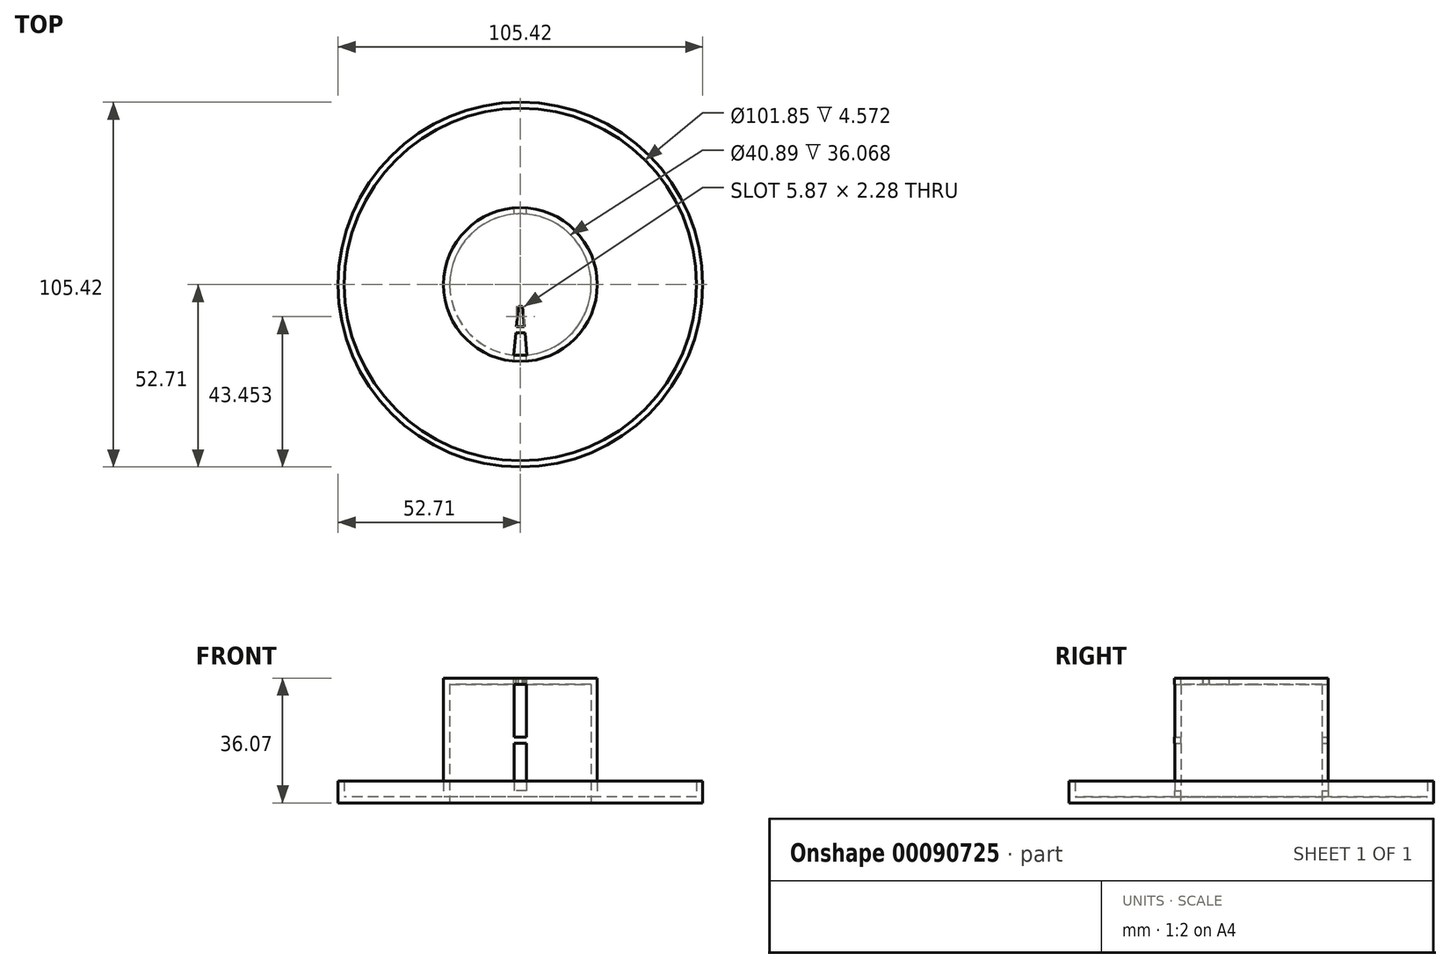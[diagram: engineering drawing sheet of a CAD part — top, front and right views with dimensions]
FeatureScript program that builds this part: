
annotation { "Feature Type Name" : "Feature", "Feature Type Description" : "" }
export const myFeature = defineFeature(function(context is Context, id is Id, definition is map)
    precondition{}
    {
        {
            var Q0;
            Q0=qCreatedBy(makeId("Top.planeOp"),FACE);
            var sketch = newSketch(context, id + "F0", { "sketchPlane" : qUnion([Q0])});
            skCircle(sketch, "E0", {"center": v(0, 0) * mm, "radius": 52.7 * mm});
            skSolve(sketch);
        }
        {
            var Q0;
            Q0 = qSketchRegion(id + "F0", true);
            extrude(context, id + "F1", {"entities" : qUnion([Q0]), "depth" : 6.35 * mm});
        }
        {
            var Q0;
            Q0=makeQuery(id+"F1.opExtrude","CAP_FACE",FACE,{"disambiguationData":[OSD([sQuery(id+"F0.wireOp",EDGE,"E0")])],"isStart":false});
            shell(context, id + "F2", {"entities" : qUnion([Q0]), "thickness" : 1.78 * mm});
        }
        {
            var Q0;
            {var subQ0=sQuery(id+"F0.wireOp",EDGE,"E0");Q0=makeQuery(id+"F2.opShell","OFFSET_FACE",FACE,{"disambiguationData":[OSD([subQ0]),TDD([makeQuery(id+"F1.opExtrude","CAP_FACE",FACE,{"disambiguationData":[OSD([subQ0])],"isStart":true})])]});}
            var sketch = newSketch(context, id + "F3", { "sketchPlane" : qUnion([Q0])});
            skCircle(sketch, "E1", {"center": v(0, 0) * mm, "radius": 22.23 * mm});
            skSolve(sketch);
        }
        {
            var Q0;
            Q0 = qSketchRegion(id + "F3", true);
            extrude(context, id + "F4", {"entities" : qUnion([Q0]), "operationType" : NewBodyOperationType.ADD, "depth" : 34.3 * mm});
        }
        {
            var Q0;
            Q0=qCreatedBy(makeId("Front.planeOp"),FACE);
            var sketch = newSketch(context, id + "F5", { "sketchPlane" : qUnion([Q0])});
            skLineSegment(sketch, "E2.bottom", {"start": v(-1.78, 34.3) * mm, "end": v(1.78, 34.3) * mm});
            skLineSegment(sketch, "E2.top", {"start": v(-1.78, 19.05) * mm, "end": v(1.78, 19.05) * mm});
            skLineSegment(sketch, "E2.left", {"start": v(-1.78, 34.3) * mm, "end": v(-1.78, 19.05) * mm});
            skLineSegment(sketch, "E2.right", {"start": v(1.78, 34.3) * mm, "end": v(1.78, 19.05) * mm});
            skLineSegment(sketch, "E3.bottom", {"start": v(-1.78, 17.27) * mm, "end": v(1.78, 17.27) * mm});
            skLineSegment(sketch, "E3.top", {"start": v(-1.78, 3.56) * mm, "end": v(1.78, 3.56) * mm});
            skLineSegment(sketch, "E3.left", {"start": v(-1.78, 17.27) * mm, "end": v(-1.78, 3.56) * mm});
            skLineSegment(sketch, "E3.right", {"start": v(1.78, 17.27) * mm, "end": v(1.78, 3.56) * mm});
            skSolve(sketch);
        }
        {
            var Q0;
            Q0 = qSketchRegion(id + "F5", true);
            var Q1;
            Q1=makeQuery(id+"F4.opExtrude","SWEPT_FACE",FACE,{"disambiguationData":[OSD([sQuery(id+"F3.wireOp",EDGE,"E1")])]});
            extrude(context, id + "F6", {"entities" : qUnion([Q0]), "operationType" : NewBodyOperationType.REMOVE, "endBoundEntityFace" : qUnion([Q1]), "depth" : 50.8 * mm, "symmetric" : true});
        }
        {
            var Q0;
            Q0=makeQuery(id+"F1.opExtrude","CAP_FACE",FACE,{"disambiguationData":[OSD([sQuery(id+"F0.wireOp",EDGE,"E0")])],"isStart":true});
            var sketch = newSketch(context, id + "F7", { "sketchPlane" : qUnion([Q0])});
            skCircle(sketch, "E4.0", {"center": v(0, 0) * mm, "radius": 22.23 * mm, "construction": true});
            skCircle(sketch, "E5.0", {"center": v(0, 0) * mm, "radius": 20.45 * mm});
            skSolve(sketch);
        }
        {
            var Q0;
            Q0 = qSketchRegion(id + "F7", true);
            extrude(context, id + "F8", {"entities" : qUnion([Q0]), "operationType" : NewBodyOperationType.REMOVE, "oppositeDirection" : true, "depth" : 34.3 * mm});
        }
        {
            var Q0;
            Q0=makeQuery(id+"F4.opExtrude","CAP_FACE",FACE,{"disambiguationData":[OSD([sQuery(id+"F3.wireOp",EDGE,"E1")])],"isStart":false});
            var sketch = newSketch(context, id + "F9", { "sketchPlane" : qUnion([Q0])});
            skArc(sketch, "E6.0", {"start": v(-1.78, -22.15) * mm, "mid": v(0, -22.23) * mm, "end": v(1.78, -22.15) * mm, "construction": true});
            skArc(sketch, "E7.0", {"start": v(-1.9, -20.36) * mm, "mid": v(0, -20.45) * mm, "end": v(1.9, -20.36) * mm});
            skLineSegment(sketch, "E8", {"start": v(-1.9, -20.36) * mm, "end": v(-1.3, -13.9) * mm});
            skLineSegment(sketch, "E9", {"start": v(1.9, -20.36) * mm, "end": v(1.3, -13.9) * mm});
            skArc(sketch, "E10", {"start": v(-1.3, -13.9) * mm, "mid": v(0, -13.97) * mm, "end": v(1.3, -13.9) * mm});
            skArc(sketch, "E11.0", {"start": v(-1.14, -12.14) * mm, "mid": v(0, -12.2) * mm, "end": v(1.14, -12.14) * mm});
            skArc(sketch, "E12", {"start": v(-0.6, -6.32) * mm, "mid": v(0, -6.35) * mm, "end": v(0.6, -6.32) * mm});
            skLineSegment(sketch, "E13", {"start": v(1.14, -12.14) * mm, "end": v(0.6, -6.32) * mm});
            skLineSegment(sketch, "E14", {"start": v(-1.14, -12.14) * mm, "end": v(-0.6, -6.32) * mm});
            skSolve(sketch);
        }
        {
            var Q0;
            Q0 = qSketchRegion(id + "F9", true);
            extrude(context, id + "F10", {"entities" : qUnion([Q0]), "operationType" : NewBodyOperationType.REMOVE, "oppositeDirection" : true, "depth" : 25.4 * mm});
        }
    });
